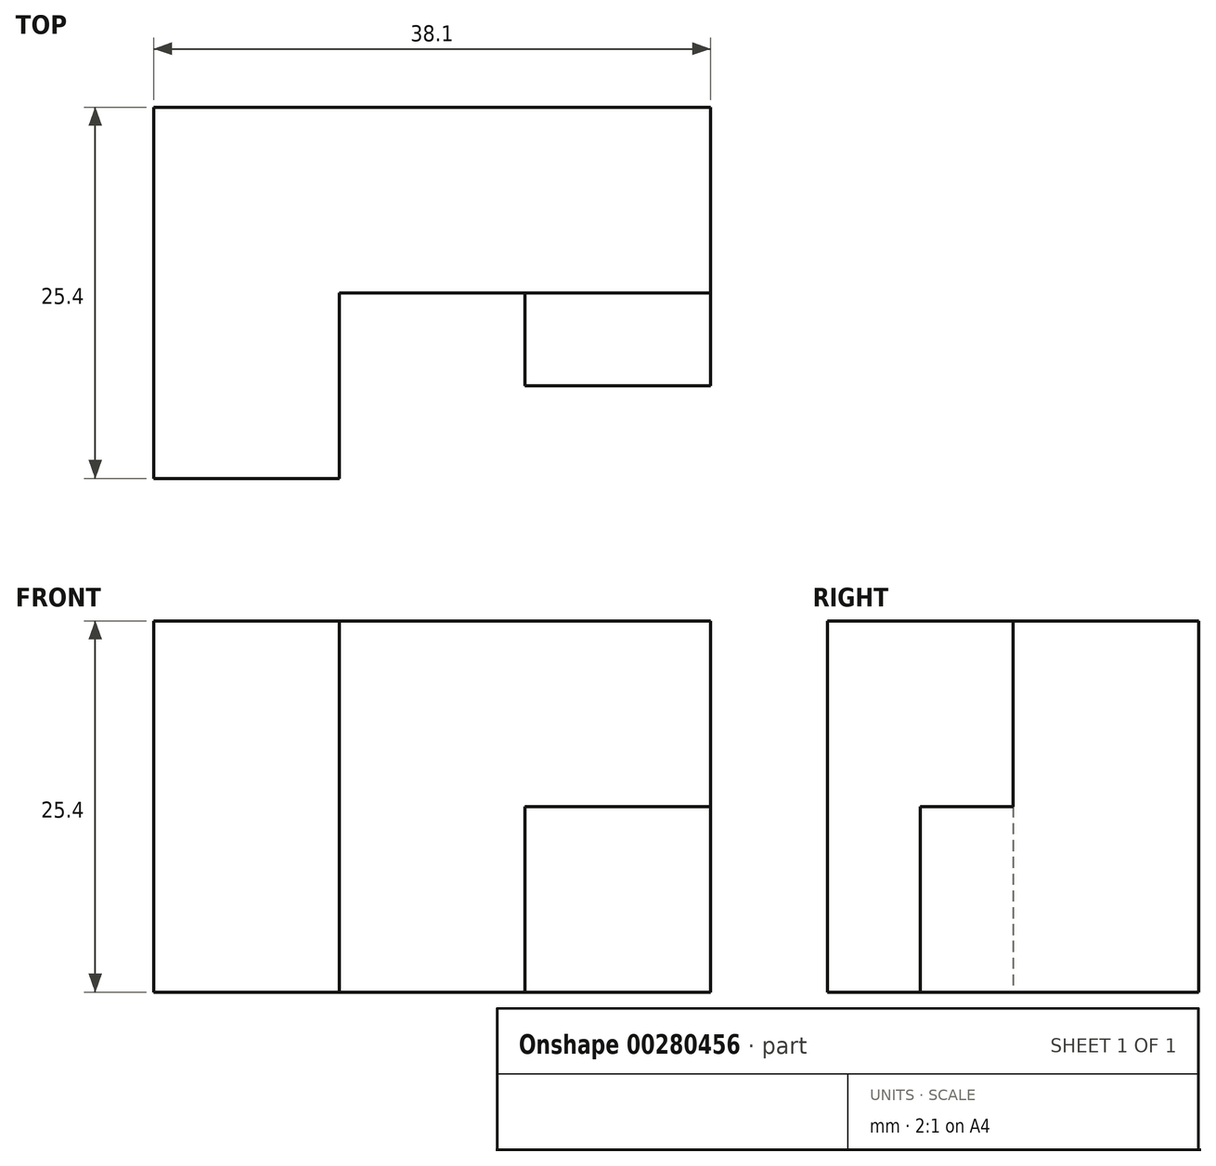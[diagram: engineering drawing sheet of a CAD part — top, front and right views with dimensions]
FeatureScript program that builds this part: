
annotation { "Feature Type Name" : "Feature", "Feature Type Description" : "" }
export const myFeature = defineFeature(function(context is Context, id is Id, definition is map)
    precondition{}
    {
        {
            var Q0;
            Q0=qCreatedBy(makeId("Top.planeOp"),FACE);
            var sketch = newSketch(context, id + "F0", { "sketchPlane" : qUnion([Q0])});
            skLineSegment(sketch, "E0.bottom", {"start": v(0, 0) * mm, "end": v(38.1, 0) * mm});
            skLineSegment(sketch, "E0.top", {"start": v(0, 25.4) * mm, "end": v(38.1, 25.4) * mm});
            skLineSegment(sketch, "E0.left", {"start": v(0, 0) * mm, "end": v(0, 25.4) * mm});
            skLineSegment(sketch, "E0.right", {"start": v(38.1, 0) * mm, "end": v(38.1, 25.4) * mm});
            skSolve(sketch);
        }
        {
            var Q0;
            Q0 = qSketchRegion(id + "F0", true);
            extrude(context, id + "F1", {"entities" : qUnion([Q0]), "depth" : 25.4 * mm});
        }
        {
            var Q0;
            Q0=makeQuery(id+"F1.opExtrude","SWEPT_FACE",FACE,{"disambiguationData":[OSD([sQuery(id+"F0.wireOp",EDGE,"E0.bottom")])]});
            var sketch = newSketch(context, id + "F2", { "sketchPlane" : qUnion([Q0])});
            skLineSegment(sketch, "E1", {"start": v(0, 25.4) * mm, "end": v(12.7, 25.4) * mm});
            skLineSegment(sketch, "E2", {"start": v(12.7, 25.4) * mm, "end": v(12.7, 0) * mm});
            skLineSegment(sketch, "E3", {"start": v(12.7, 0) * mm, "end": v(25.4, 0) * mm});
            skLineSegment(sketch, "E4", {"start": v(25.4, 0) * mm, "end": v(25.4, 12.7) * mm});
            skLineSegment(sketch, "E5", {"start": v(25.4, 12.7) * mm, "end": v(38.1, 12.7) * mm});
            skLineSegment(sketch, "E6", {"start": v(38.1, 12.7) * mm, "end": v(38.1, 25.4) * mm});
            skLineSegment(sketch, "E7", {"start": v(38.1, 25.4) * mm, "end": v(12.7, 25.4) * mm});
            skSolve(sketch);
        }
        {
            var Q0;
            Q0 = qSketchRegion(id + "F2", true);
            extrude(context, id + "F3", {"entities" : qUnion([Q0]), "operationType" : NewBodyOperationType.REMOVE, "oppositeDirection" : true, "depth" : 12.7 * mm});
        }
        {
            var Q0;
            {var subQ0=sQuery(id+"F0.wireOp",EDGE,"E0.right");var subQ1=sQuery(id+"F0.wireOp",EDGE,"E0.bottom");Q0=makeQuery(id+"F3.boolean.opBoolean","SPLIT",FACE,{"disambiguationData":[TD([makeQuery(id+"F1.opExtrude","SWEPT_FACE",FACE,{"disambiguationData":[OSD([subQ0])]})])],"derivedFrom":makeQuery(id+"F1.opExtrude","SWEPT_FACE",FACE,{"disambiguationData":[OSD([subQ1])]})});}
            var sketch = newSketch(context, id + "F4", { "sketchPlane" : qUnion([Q0])});
            skLineSegment(sketch, "E8.bottom", {"start": v(38.1, 0) * mm, "end": v(25.4, 0) * mm});
            skLineSegment(sketch, "E8.top", {"start": v(38.1, 12.7) * mm, "end": v(25.4, 12.7) * mm});
            skLineSegment(sketch, "E8.left", {"start": v(38.1, 0) * mm, "end": v(38.1, 12.7) * mm});
            skLineSegment(sketch, "E8.right", {"start": v(25.4, 0) * mm, "end": v(25.4, 12.7) * mm});
            skSolve(sketch);
        }
        {
            var Q0;
            Q0 = qSketchRegion(id + "F4", true);
            extrude(context, id + "F5", {"entities" : qUnion([Q0]), "operationType" : NewBodyOperationType.REMOVE, "oppositeDirection" : true, "depth" : 6.35 * mm});
        }
    });
